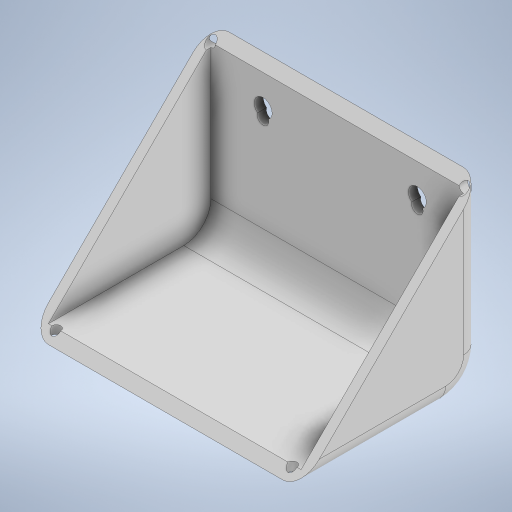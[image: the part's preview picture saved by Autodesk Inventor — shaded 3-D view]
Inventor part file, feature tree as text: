
AUTODESK INVENTOR PART (.ipt)
format: ipt  version: 2023 (Build 270158000, 158)  size: 293,376 bytes
history: native  units: in
note: dims shown in document units (in); Inventor stores cm internally (conversion verified against a paired STEP export)
features: sketch x6, extrude x4, shell x2, fillet x2, hole x2
ambient origin geometry x8: Origin, YZ Plane, XZ Plane, XY Plane, X Axis, Y Axis, Z Axis, Center Point
bodies: Solid1 (feature_tree)
feature tree (16):
  shell  "shell"  Thickness=5.0in
  extrude  "Extrusion1"  Depth=0.25in TaperAngle=0.0deg
  fillet  "Fillet1"  Radius=1.0in
  shell  "Shell1"  Thickness=0.25in
  fillet  "Fillet2"  Radius=0.5in
  extrude  "Extrusion2"  Depth=0.25in
  extrude  "Extrusion3"  Depth=0.5in
  extrude  "Extrusion4"  Depth=1.0in TaperAngle=0.0deg
  hole  "Hole1"  [1 undecoded]
  hole  "Hole2"  [1 undecoded]
  sketch  "Sketch1"  dims[d1=5.0in d2=7.5in d3=0.0in d4=1.0in d5=0.25in d6=0.5in]
  sketch  "Sketch2"  dims[d7=0.25in d8=2.5in]
  sketch  "Sketch3"  dims[d9=1.0in d10=0.0in d11=0.5in]
  sketch  "Sketch4"  dims[d12=0.5in d13=1.0in d14=0.0in]
  sketch  "Sketch5"  dims[d15=0.325in d16=0.325in]
  sketch  "Sketch6"  dims[d17=1.0in d18=0.0in d19=0.25in d20=0.75in d21=0.375in d22=0.25in d23=0.5635in d24=1.0in d25=0.8108in d26=0.25in d27=0.75in d28=0.375in d29=0.25in d30=0.5635in d31=1.0in d32=0.8108in]
note: 2 required parameter values undecoded (feature->parameter linkage not recoverable at this tier; creation-order binding heuristic only, values carry confidence <= 0.55)
